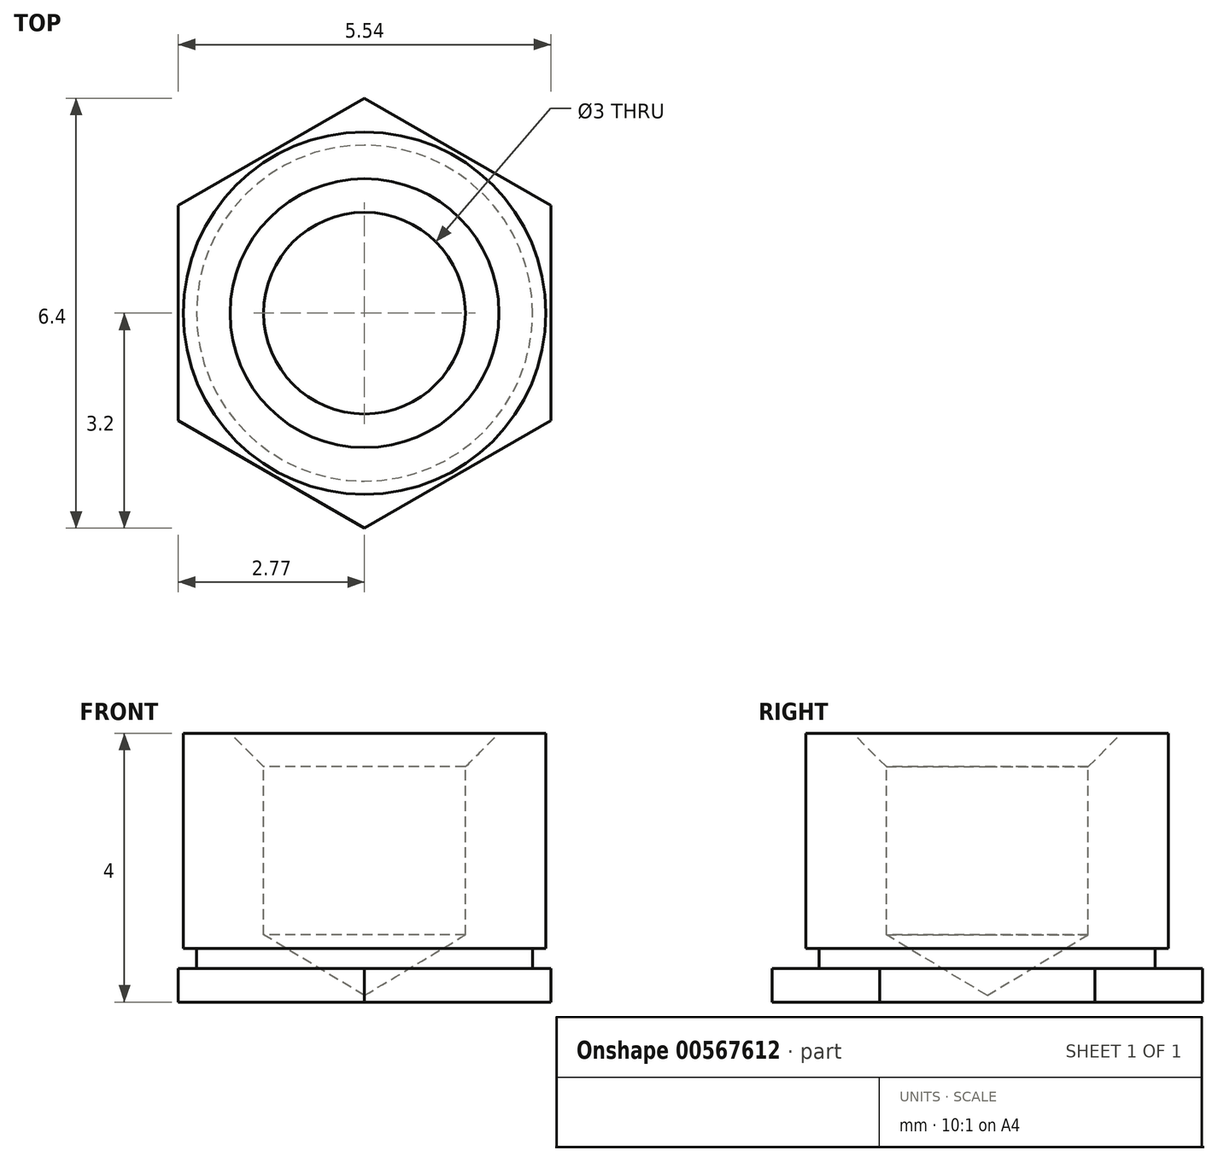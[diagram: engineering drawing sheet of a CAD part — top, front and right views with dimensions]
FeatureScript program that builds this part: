
annotation { "Feature Type Name" : "Feature", "Feature Type Description" : "" }
export const myFeature = defineFeature(function(context is Context, id is Id, definition is map)
    precondition{}
    {
        {
            var Q0;
            Q0=qCreatedBy(makeId("Top.planeOp"),FACE);
            var sketch = newSketch(context, id + "F0", { "sketchPlane" : qUnion([Q0])});
            skCircle(sketch, "E0.cCircle", {"center": v(0, 0) * mm, "radius": 3.2 * mm, "construction": true});
            skLineSegment(sketch, "E0.0", {"start": v(0, -3.2) * mm, "end": v(-2.77, -1.6) * mm});
            skLineSegment(sketch, "E0.1", {"start": v(-2.77, -1.6) * mm, "end": v(-2.77, 1.6) * mm});
            skLineSegment(sketch, "E0.2", {"start": v(-2.77, 1.6) * mm, "end": v(0, 3.2) * mm});
            skLineSegment(sketch, "E0.3", {"start": v(0, 3.2) * mm, "end": v(2.77, 1.6) * mm});
            skLineSegment(sketch, "E0.4", {"start": v(2.77, 1.6) * mm, "end": v(2.77, -1.6) * mm});
            skLineSegment(sketch, "E0.5", {"start": v(2.77, -1.6) * mm, "end": v(0, -3.2) * mm});
            skSolve(sketch);
        }
        {
            var Q0;
            Q0=qSketchRegion(id+"F0",true);
            extrude(context, id + "F1", {"entities" : qUnion([Q0]), "depth" : 0.5 * mm, "offsetDistance" : 25 * mm});
        }
        {
            var Q0;
            Q0=makeQuery(id+"F1.opExtrude","CAP_FACE",FACE,{"disambiguationData":[OSD([sQuery(id+"F0.wireOp",EDGE,"E0.0"),sQuery(id+"F0.wireOp",EDGE,"E0.1"),sQuery(id+"F0.wireOp",EDGE,"E0.2"),sQuery(id+"F0.wireOp",EDGE,"E0.3"),sQuery(id+"F0.wireOp",EDGE,"E0.4"),sQuery(id+"F0.wireOp",EDGE,"E0.5")])],"isStart":false});
            var sketch = newSketch(context, id + "F2", { "sketchPlane" : qUnion([Q0])});
            skCircle(sketch, "E1", {"center": v(0, 0) * mm, "radius": 2.5 * mm});
            skSolve(sketch);
        }
        {
            var Q0;
            Q0=qSketchRegion(id+"F2",true);
            extrude(context, id + "F3", {"entities" : qUnion([Q0]), "operationType" : NewBodyOperationType.ADD, "depth" : 0.3 * mm, "offsetDistance" : 25 * mm});
        }
        {
            var Q0;
            Q0=makeQuery(id+"F3.opExtrude","CAP_FACE",FACE,{"disambiguationData":[OSD([sQuery(id+"F2.wireOp",EDGE,"E1")])],"isStart":false});
            var sketch = newSketch(context, id + "F4", { "sketchPlane" : qUnion([Q0])});
            skCircle(sketch, "E2", {"center": v(0, 0) * mm, "radius": 2.7 * mm});
            skSolve(sketch);
        }
        {
            var Q0;
            Q0=qSketchRegion(id+"F4",true);
            extrude(context, id + "F5", {"entities" : qUnion([Q0]), "operationType" : NewBodyOperationType.ADD, "depth" : (4 - 0.8) * mm, "offsetDistance" : 25 * mm});
        }
        {
            var Q0;
            Q0=makeQuery(id+"F5.opExtrude","CAP_FACE",FACE,{"disambiguationData":[OSD([sQuery(id+"F4.wireOp",EDGE,"E2")])],"isStart":false});
            var sketch = newSketch(context, id + "F6", { "sketchPlane" : qUnion([Q0])});
            skCircle(sketch, "E3.0", {"center": v(0, 0) * mm, "radius": 2.7 * mm});
            skSolve(sketch);
        }
        {
            var Q0;
            Q0=sQuery(id+"F6.wireOp",VERTEX,"E3.0.center");
            var Q1;
            Q1=makeQuery(id+"F1.opExtrude","SWEPT_BODY",BODY,{"disambiguationData":[OSD([sQuery(id+"F0.wireOp",EDGE,"E0.0"),sQuery(id+"F0.wireOp",EDGE,"E0.1"),sQuery(id+"F0.wireOp",EDGE,"E0.2"),sQuery(id+"F0.wireOp",EDGE,"E0.3"),sQuery(id+"F0.wireOp",EDGE,"E0.4"),sQuery(id+"F0.wireOp",EDGE,"E0.5")])]});
            hole(context, id + "F7", {"style" : HoleStyle.C_SINK, "endStyle" : HoleEndStyle.BLIND, "holeDiameter" : 3 * mm, "cSinkDiameter" : 4 * mm, "cSinkAngle" : 90 * degree, "holeDepth" : 3 * mm, "isTappedThrough" : true, "tappedDepth" : 12 * mm, "tapClearance" : 3, "locations" : qUnion([Q0]), "scope" : qUnion([Q1])});
        }
    });
